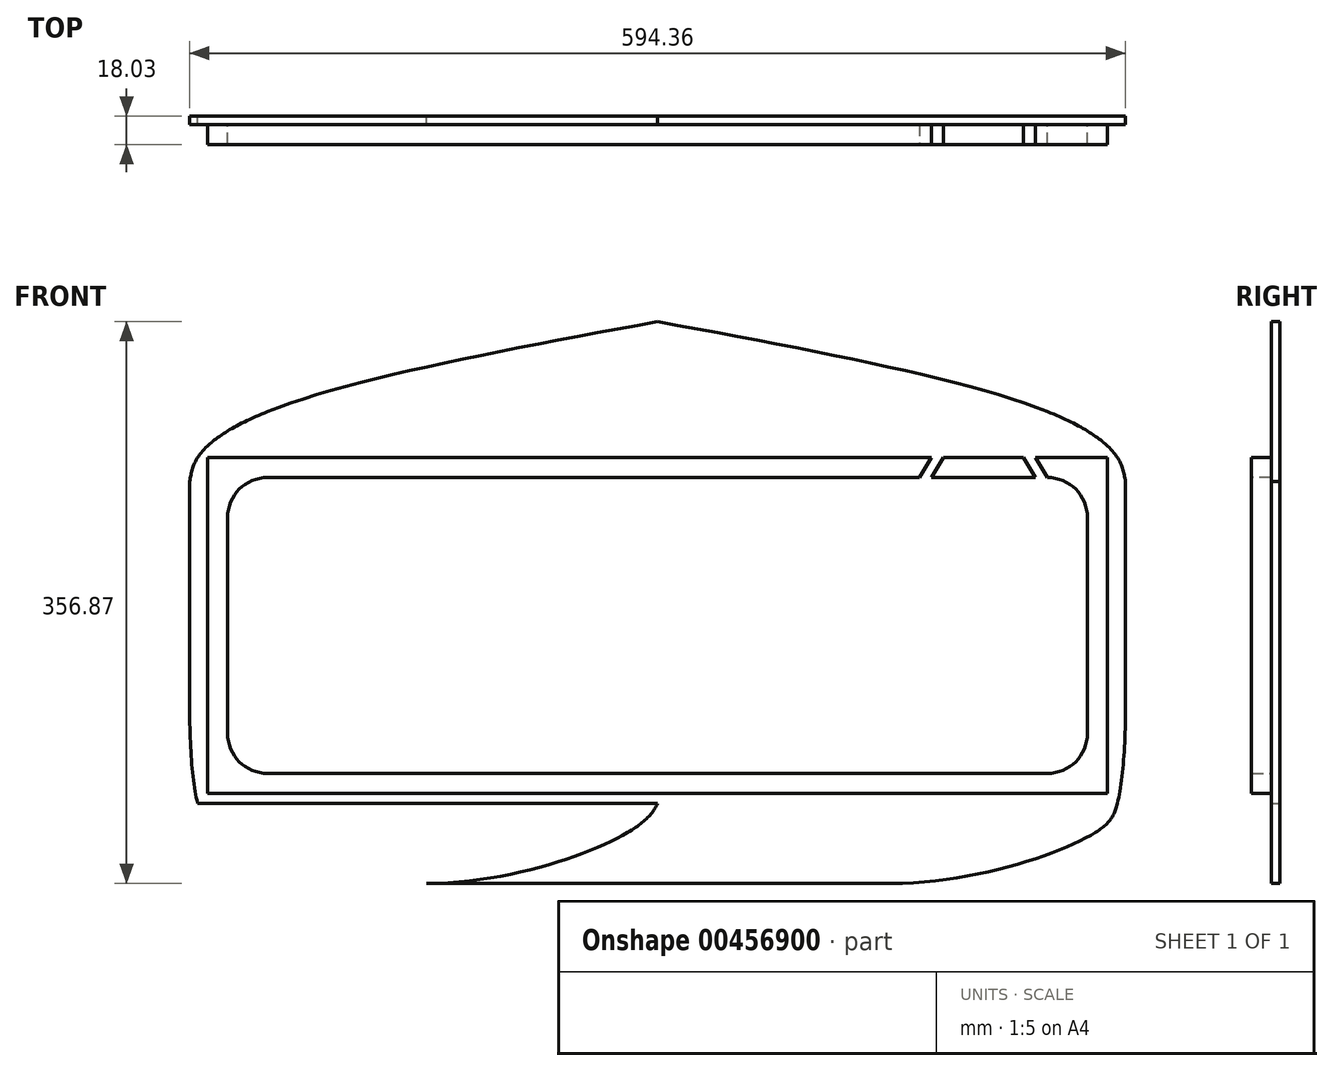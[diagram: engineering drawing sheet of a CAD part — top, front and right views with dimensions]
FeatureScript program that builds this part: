
annotation { "Feature Type Name" : "Feature", "Feature Type Description" : "" }
export const myFeature = defineFeature(function(context is Context, id is Id, definition is map)
    precondition{}
    {
        {
            var Q0;
            Q0=qCreatedBy(makeId("Front.planeOp"),FACE);
            var sketch = newSketch(context, id + "F0", { "sketchPlane" : qUnion([Q0])});
            skLineSegment(sketch, "E0.bottom", {"start": v(0, 0) * mm, "end": v(-584.2, 0) * mm});
            skLineSegment(sketch, "E0.top", {"start": v(0, 219.7) * mm, "end": v(-584.2, 219.7) * mm});
            skLineSegment(sketch, "E0.left", {"start": v(0, 0) * mm, "end": v(0, 219.7) * mm});
            skLineSegment(sketch, "E0.right", {"start": v(-584.2, 0) * mm, "end": v(-584.2, 219.7) * mm});
            skPoint(sketch, "E1", {"position": v(-292.1, 219.7) * mm});
            skSolve(sketch);
        }
        {
            var Q0;
            Q0=makeQuery(id+"F0.imprint","IMPRINT",FACE,{"disambiguationData":[TD([[makeQuery(id+"F0.imprint","IMPRINT",EDGE,{"derivedFrom":sQuery(id+"F0.wireOp",EDGE,"E0.bottom")}),-1.0]])]});
            extrude(context, id + "F1", {"entities" : qUnion([Q0]), "depth" : 5.33 * mm});
        }
        {
            var Q0;
            Q0=makeQuery(id+"F1.opExtrude","CAP_FACE",FACE,{"disambiguationData":[OSD([sQuery(id+"F0.wireOp",EDGE,"E0.bottom"),sQuery(id+"F0.wireOp",EDGE,"E0.top"),sQuery(id+"F0.wireOp",EDGE,"E0.left"),sQuery(id+"F0.wireOp",EDGE,"E0.right")])],"isStart":false});
            var sketch = newSketch(context, id + "F2", { "sketchPlane" : qUnion([Q0])});
            skLineSegment(sketch, "E2", {"start": v(-577.85, 219.7) * mm, "end": v(-577.85, 6.35) * mm});
            skLineSegment(sketch, "E3", {"start": v(-577.85, 6.35) * mm, "end": v(-6.35, 6.35) * mm});
            skLineSegment(sketch, "E4", {"start": v(-6.35, 6.35) * mm, "end": v(-6.35, 219.71) * mm});
            skLineSegment(sketch, "E5", {"start": v(-6.35, 219.71) * mm, "end": v(-577.85, 219.7) * mm});
            skLineSegment(sketch, "E6", {"start": v(-565.15, 207) * mm, "end": v(-565.15, 19.05) * mm});
            skLineSegment(sketch, "E7", {"start": v(-565.15, 19.05) * mm, "end": v(-19.05, 19.05) * mm});
            skLineSegment(sketch, "E8", {"start": v(-19.05, 19.05) * mm, "end": v(-19.05, 207.01) * mm});
            skLineSegment(sketch, "E9", {"start": v(-19.05, 207.01) * mm, "end": v(-565.15, 207) * mm});
            skSolve(sketch);
        }
        {
            var Q0;
            Q0=makeQuery(id+"F2.imprint","IMPRINT",FACE,{"disambiguationData":[TD([[makeQuery(id+"F2.imprint","IMPRINT",EDGE,{"derivedFrom":sQuery(id+"F2.wireOp",EDGE,"E2")}),1.0]])]});
            extrude(context, id + "F3", {"entities" : qUnion([Q0]), "operationType" : NewBodyOperationType.ADD, "depth" : 12.7 * mm});
        }
        {
            var Q0;
            Q0=makeQuery(id+"F3.opExtrude","SWEPT_EDGE",EDGE,{"disambiguationData":[OSD([sQuery(id+"F2.wireOp",EDGE,"E6"),sQuery(id+"F2.wireOp",EDGE,"E9")])]});
            var Q1;
            Q1=makeQuery(id+"F3.opExtrude","SWEPT_EDGE",EDGE,{"disambiguationData":[OSD([sQuery(id+"F2.wireOp",EDGE,"E8"),sQuery(id+"F2.wireOp",EDGE,"E9")])]});
            var Q2;
            Q2=makeQuery(id+"F3.opExtrude","SWEPT_EDGE",EDGE,{"disambiguationData":[OSD([sQuery(id+"F2.wireOp",EDGE,"E7"),sQuery(id+"F2.wireOp",EDGE,"E8")])]});
            var Q3;
            Q3=makeQuery(id+"F3.opExtrude","SWEPT_EDGE",EDGE,{"disambiguationData":[OSD([sQuery(id+"F2.wireOp",EDGE,"E6"),sQuery(id+"F2.wireOp",EDGE,"E7")])]});
            fillet(context, id + "F4", {"entities" : qUnion([Q0, Q1, Q2, Q3]), "radius" : 25.4 * mm, "tangentPropagation" : true, "allowEdgeOverflow" : false});
        }
        {
            var Q0;
            Q0=makeQuery(id+"F3.opExtrude","CAP_FACE",FACE,{"disambiguationData":[OSD([sQuery(id+"F2.wireOp",EDGE,"E2"),sQuery(id+"F2.wireOp",EDGE,"E3"),sQuery(id+"F2.wireOp",EDGE,"E4"),sQuery(id+"F2.wireOp",EDGE,"E5"),sQuery(id+"F2.wireOp",EDGE,"E6"),sQuery(id+"F2.wireOp",EDGE,"E7"),sQuery(id+"F2.wireOp",EDGE,"E8"),sQuery(id+"F2.wireOp",EDGE,"E9")])],"isStart":false});
            var sketch = newSketch(context, id + "F5", { "sketchPlane" : qUnion([Q0])});
            skPoint(sketch, "E10", {"position": v(-118.11, 219.7) * mm});
            skPoint(sketch, "E11", {"position": v(-110.5, 219.7) * mm});
            skPoint(sketch, "E12", {"position": v(-59.69, 219.7) * mm});
            skPoint(sketch, "E13", {"position": v(-52.07, 219.7) * mm});
            skPoint(sketch, "E14", {"position": v(-376.28, 272.75) * mm});
            skPoint(sketch, "E15", {"position": v(-12.7, 0) * mm});
            skPoint(sketch, "E16", {"position": v(-20.32, 0) * mm});
            skLineSegment(sketch, "E17", {"start": v(-20.32, 0) * mm, "end": v(-12.7, 0) * mm});
            skPoint(sketch, "E18", {"position": v(-118.11, 207.01) * mm});
            skPoint(sketch, "E19", {"position": v(-125.73, 207.01) * mm});
            skLineSegment(sketch, "E20", {"start": v(-125.73, 207.01) * mm, "end": v(-118.11, 219.7) * mm});
            skLineSegment(sketch, "E21", {"start": v(-125.73, 207.01) * mm, "end": v(-118.11, 207.01) * mm});
            skLineSegment(sketch, "E22", {"start": v(-118.11, 207.01) * mm, "end": v(-110.5, 219.7) * mm});
            skLineSegment(sketch, "E23", {"start": v(-118.11, 219.7) * mm, "end": v(-110.5, 219.7) * mm});
            skLineSegment(sketch, "E24", {"start": v(-59.69, 219.7) * mm, "end": v(-52.07, 219.7) * mm});
            skLineSegment(sketch, "E25", {"start": v(-110.5, 219.7) * mm, "end": v(-59.69, 219.7) * mm});
            skLineSegment(sketch, "E26", {"start": v(-59.69, 219.7) * mm, "end": v(-110.5, 219.7) * mm});
            skLineSegment(sketch, "E27", {"start": v(-110.5, 219.7) * mm, "end": v(-113.58, 214.56) * mm});
            skPoint(sketch, "E28", {"position": v(-44.45, 207.01) * mm});
            skPoint(sketch, "E29", {"position": v(-52.07, 207.01) * mm});
            skLineSegment(sketch, "E30", {"start": v(-59.69, 219.7) * mm, "end": v(-52.07, 207.01) * mm});
            skLineSegment(sketch, "E31", {"start": v(-52.07, 219.7) * mm, "end": v(-44.45, 207.01) * mm});
            skLineSegment(sketch, "E32", {"start": v(-52.07, 207.01) * mm, "end": v(-44.45, 207.01) * mm});
            skLineSegment(sketch, "E33", {"start": v(-52.07, 219.7) * mm, "end": v(-59.69, 219.7) * mm});
            skPoint(sketch, "E34", {"position": v(-56.6, 214.56) * mm});
            skLineSegment(sketch, "E35", {"start": v(-113.58, 214.56) * mm, "end": v(-56.6, 214.56) * mm});
            skSolve(sketch);
        }
        {
            var Q0;
            Q0=makeQuery(id+"F5.imprint","IMPRINT",FACE,{"disambiguationData":[TD([[makeQuery(id+"F5.imprint","IMPRINT",EDGE,{"derivedFrom":sQuery(id+"F5.wireOp",EDGE,"E20")}),-1.0]])]});
            var Q1;
            {var subQ8=sQuery(id+"F5.wireOp",EDGE,"RZINdJYM-ykuw-GilU-JIjt-DnibDYUsXZuo");Q1=makeQuery(id+"F5.imprint","IMPRINT",FACE,{"disambiguationData":[TD([[makeQuery(id+"F5.imprint","IMPRINT",EDGE,{"derivedFrom":subQ8}),1.0]])]});}
            var Q2;
            Q2=makeQuery(id+"F5.imprint","IMPRINT",FACE,{"disambiguationData":[TD([[makeQuery(id+"F5.imprint","IMPRINT",EDGE,{"derivedFrom":sQuery(id+"F5.wireOp",EDGE,"RZINdJYM-ykuw-GilU-JIjt-DnibDYUsXZuo")}),-1.0]])]});
            var Q3;
            Q3=makeQuery(id+"F5.imprint","IMPRINT",FACE,{"disambiguationData":[TD([[makeQuery(id+"F5.imprint","IMPRINT",EDGE,{"derivedFrom":sQuery(id+"F5.wireOp",EDGE,"NQJIxGkc-Vixr-o2zM-VUe3-bVQ5EoZFKsab")}),1.0]])]});
            var Q4;
            Q4=makeQuery(id+"F5.imprint","IMPRINT",FACE,{"disambiguationData":[TD([[makeQuery(id+"F5.imprint","IMPRINT",EDGE,{"derivedFrom":sQuery(id+"F5.wireOp",EDGE,"E30")}),1.0]])]});
            var Q5;
            {var subQ0=sQuery(id+"F5.wireOp",EDGE,"E26");Q5=makeQuery(id+"F5.imprint","IMPRINT",FACE,{"disambiguationData":[TD([[makeQuery(id+"F5.imprint","IMPRINT",EDGE,{"derivedFrom":subQ0}),1.0]])]});}
            extrude(context, id + "F6", {"entities" : qUnion([Q0, Q1, Q2, Q3, Q4, Q5]), "operationType" : NewBodyOperationType.REMOVE, "oppositeDirection" : true, "depth" : 12.7 * mm});
        }
        {
            var Q0;
            Q0=makeQuery(id+"F1.opExtrude","CAP_FACE",FACE,{"disambiguationData":[OSD([sQuery(id+"F0.wireOp",EDGE,"E0.bottom"),sQuery(id+"F0.wireOp",EDGE,"E0.top"),sQuery(id+"F0.wireOp",EDGE,"E0.left"),sQuery(id+"F0.wireOp",EDGE,"E0.right")])],"isStart":true});
            var sketch = newSketch(context, id + "F7", { "sketchPlane" : qUnion([Q0])});
            skLineSegment(sketch, "E36", {"start": v(0, 0) * mm, "end": v(-5.08, 0) * mm});
            skLineSegment(sketch, "E37", {"start": v(-5.08, 0) * mm, "end": v(-5.08, 229.87) * mm});
            skLineSegment(sketch, "E38", {"start": v(-5.08, 229.87) * mm, "end": v(589.28, 229.87) * mm});
            skLineSegment(sketch, "E39", {"start": v(589.28, 229.87) * mm, "end": v(589.28, 0) * mm});
            skLineSegment(sketch, "E40", {"start": v(589.28, 0) * mm, "end": v(584.2, 0) * mm});
            skPoint(sketch, "E41", {"position": v(589.28, 114.93) * mm});
            skPoint(sketch, "E42", {"position": v(584.2, 109.85) * mm});
            skPoint(sketch, "E43", {"position": v(292.1, 229.87) * mm});
            skPoint(sketch, "E44", {"position": v(292.1, 219.7) * mm});
            skPoint(sketch, "E45", {"position": v(-5.08, 114.94) * mm});
            skPoint(sketch, "E46", {"position": v(0, 109.85) * mm});
            skPoint(sketch, "E47", {"position": v(538.48, 229.87) * mm});
            skPoint(sketch, "E48", {"position": v(45.72, 229.87) * mm});
            skPoint(sketch, "E49", {"position": v(-5.08, 204.47) * mm});
            skPoint(sketch, "E50", {"position": v(589.28, 204.47) * mm});
            skPoint(sketch, "E51", {"position": v(584.2, 183.25) * mm});
            skPoint(sketch, "E52", {"position": v(0, 176.13) * mm});
            skPoint(sketch, "E53", {"position": v(589.28, 63.5) * mm});
            skPoint(sketch, "E54", {"position": v(-5.08, 63.5) * mm});
            skPoint(sketch, "E55", {"position": v(0, 219.7) * mm});
            skPoint(sketch, "E56", {"position": v(584.2, 219.7) * mm});
            skPoint(sketch, "E57", {"position": v(393.7, 219.7) * mm});
            skPoint(sketch, "E58", {"position": v(190.5, 219.7) * mm});
            skLineSegment(sketch, "E59", {"start": v(292.1, 219.7) * mm, "end": v(-5.08, 229.87) * mm});
            skLineSegment(sketch, "E60", {"start": v(292.1, 219.7) * mm, "end": v(589.28, 229.87) * mm});
            skLineSegment(sketch, "E61", {"start": v(589.28, -18.42) * mm, "end": v(-5.08, -18.42) * mm});
            skLineSegment(sketch, "E62", {"start": v(589.28, 0) * mm, "end": v(589.28, -18.42) * mm});
            skLineSegment(sketch, "E63", {"start": v(292.1, 229.87) * mm, "end": v(292.1, 306.07) * mm});
            skPoint(sketch, "E64", {"position": v(292.1, -18.42) * mm});
            skLineSegment(sketch, "E65", {"start": v(589.28, -18.42) * mm, "end": v(589.28, -50.8) * mm});
            skLineSegment(sketch, "E66", {"start": v(589.28, -50.8) * mm, "end": v(292.1, -50.8) * mm});
            skPoint(sketch, "E67", {"position": v(292.1, 0) * mm});
            skPoint(sketch, "E68", {"position": v(440.7, -50.8) * mm});
            skLineSegment(sketch, "E69", {"start": v(292.1, -50.8) * mm, "end": v(-5.08, -50.8) * mm});
            skLineSegment(sketch, "E70", {"start": v(-5.08, -50.8) * mm, "end": v(-5.08, -18.42) * mm});
            skPoint(sketch, "E71", {"position": v(143.51, -50.8) * mm});
            skPoint(sketch, "E72", {"position": v(570.23, -18.42) * mm});
            skPoint(sketch, "E73", {"position": v(13.97, -18.42) * mm});
            skPoint(sketch, "E74", {"position": v(6.35, 219.7) * mm});
            skPoint(sketch, "E75", {"position": v(577.85, 219.7) * mm});
            skPoint(sketch, "E76", {"position": v(6.35, 0) * mm});
            skPoint(sketch, "E77", {"position": v(577.85, 0) * mm});
            skPoint(sketch, "E78", {"position": v(44.45, 229.87) * mm});
            skPoint(sketch, "E79", {"position": v(539.75, 229.87) * mm});
            skLineSegment(sketch, "E80", {"start": v(44.45, 229.87) * mm, "end": v(44.45, 248.92) * mm});
            skLineSegment(sketch, "E81", {"start": v(539.75, 229.87) * mm, "end": v(539.75, 248.92) * mm});
            skLineSegment(sketch, "E82", {"start": v(292.1, 0) * mm, "end": v(292.1, 6.35) * mm});
            skPoint(sketch, "E83", {"position": v(311.15, -18.42) * mm});
            skPoint(sketch, "E84", {"position": v(273.05, -18.42) * mm});
            skLineSegment(sketch, "E85", {"start": v(0, 109.85) * mm, "end": v(-44.45, 109.85) * mm});
            skLineSegment(sketch, "E86", {"start": v(584.2, 109.85) * mm, "end": v(628.65, 109.85) * mm});
            skLineSegment(sketch, "E87", {"start": v(-44.45, 109.85) * mm, "end": v(-44.45, 84.45) * mm});
            skLineSegment(sketch, "E88", {"start": v(-5.08, 0) * mm, "end": v(-5.08, -18.42) * mm});
            skLineSegment(sketch, "E89", {"start": v(628.65, 109.85) * mm, "end": v(628.65, 84.45) * mm});
            skFitSpline(sketch, "E90", {"points": [v(292.1, 0) * mm, v(311.15, -18.42) * mm, v(440.7, -50.8) * mm, v(570.23, -18.42) * mm, v(584.2, 0) * mm, v(589.28, 63.5) * mm], "startDerivative": vector(75.38, -162.05) * mm, "endDerivative": vector(-1.2, 379.78) * mm});
            skFitSpline(sketch, "E91", {"points": [v(292.1, 0) * mm, v(273.05, -18.42) * mm, v(143.51, -50.8) * mm, v(13.97, -18.42) * mm, v(0, 0) * mm, v(-5.08, 63.5) * mm], "startDerivative": vector(-102.03, -153.51) * mm, "endDerivative": vector(1.16, 380.73) * mm});
            skFitSpline(sketch, "E92", {"points": [v(292.1, 306.07) * mm, v(539.75, 248.92) * mm, v(584.2, 219.7) * mm, v(589.28, 204.47) * mm], "startDerivative": vector(500.8, -92.88) * mm, "endDerivative": vector(17.5, -102.22) * mm});
            skFitSpline(sketch, "E93", {"points": [v(292.1, 306.07) * mm, v(44.45, 248.92) * mm, v(0, 219.7) * mm, v(-5.08, 204.47) * mm], "startDerivative": vector(-500.8, -92.88) * mm, "endDerivative": vector(-17.5, -102.22) * mm});
            skSolve(sketch);
        }
        {
            var Q0;
            {var subQ0=sQuery(id+"F7.wireOp",EDGE,"E91");var subQ1=sQuery(id+"F7.wireOp",EDGE,"E61");var subQ2=makeQuery(id+"F7.imprint","INTERSECT",VERTEX,{"disambiguationData":[OD(0.0)],"derivedFrom":[subQ1,subQ0]});Q0=makeQuery(id+"F7.imprint","IMPRINT",FACE,{"disambiguationData":[TD([[makeQuery(id+"F7.imprint","IMPRINT",EDGE,{"disambiguationData":[TD([[subQ2,-1.0]])],"derivedFrom":subQ1}),-1.0]])]});}
            var Q1;
            {var subQ0=sQuery(id+"F7.wireOp",EDGE,"E91");var subQ1=sQuery(id+"F7.wireOp",EDGE,"E61");var subQ2=makeQuery(id+"F7.imprint","INTERSECT",VERTEX,{"disambiguationData":[OD(0.0)],"derivedFrom":[subQ1,subQ0]});Q1=makeQuery(id+"F7.imprint","IMPRINT",FACE,{"disambiguationData":[TD([[makeQuery(id+"F7.imprint","IMPRINT",EDGE,{"disambiguationData":[TD([[subQ2,-1.0]])],"derivedFrom":subQ1}),1.0]])]});}
            var Q2;
            {var subQ0=sQuery(id+"F7.wireOp",EDGE,"E90");var subQ1=sQuery(id+"F7.wireOp",EDGE,"E61");var subQ2=makeQuery(id+"F7.imprint","INTERSECT",VERTEX,{"disambiguationData":[OD(0.0)],"derivedFrom":[subQ1,subQ0]});Q2=makeQuery(id+"F7.imprint","IMPRINT",FACE,{"disambiguationData":[TD([[makeQuery(id+"F7.imprint","IMPRINT",EDGE,{"disambiguationData":[TD([[subQ2,-1.0]])],"derivedFrom":subQ1}),-1.0]])]});}
            var Q3;
            {var subQ0=sQuery(id+"F7.wireOp",EDGE,"E90");var subQ1=sQuery(id+"F7.wireOp",EDGE,"E61");var subQ2=makeQuery(id+"F7.imprint","INTERSECT",VERTEX,{"disambiguationData":[OD(0.0)],"derivedFrom":[subQ1,subQ0]});Q3=makeQuery(id+"F7.imprint","IMPRINT",FACE,{"disambiguationData":[TD([[makeQuery(id+"F7.imprint","IMPRINT",EDGE,{"disambiguationData":[TD([[subQ2,-1.0]])],"derivedFrom":subQ1}),1.0]])]});}
            var Q4;
            {var subQ0=sQuery(id+"F7.wireOp",EDGE,"E91");var subQ3=sQuery(id+"F7.wireOp",EDGE,"E37");var subQ8=makeQuery(id+"F7.imprint","INTERSECT",VERTEX,{"disambiguationData":[OD(0.0)],"derivedFrom":[subQ3,subQ0]});Q4=makeQuery(id+"F7.imprint","IMPRINT",FACE,{"disambiguationData":[TD([[makeQuery(id+"F7.imprint","IMPRINT",EDGE,{"disambiguationData":[TD([[subQ8,1.0]])],"derivedFrom":subQ3}),-1.0]])]});}
            var Q5;
            {var subQ0=sQuery(id+"F7.wireOp",EDGE,"ab0071de-1401-4d7e-944b-b81abdc96300");var subQ1=sQuery(id+"F7.wireOp",EDGE,"E37");var subQ2=makeQuery(id+"F7.imprint","INTERSECT",VERTEX,{"derivedFrom":[subQ1,subQ0]});Q5=makeQuery(id+"F7.imprint","IMPRINT",FACE,{"disambiguationData":[TD([[makeQuery(id+"F7.imprint","IMPRINT",EDGE,{"disambiguationData":[TD([[subQ2,1.0]])],"derivedFrom":subQ1}),-1.0]])]});}
            var Q6;
            {var subQ0=sQuery(id+"F7.wireOp",EDGE,"E59");var subQ3=sQuery(id+"F7.wireOp",EDGE,"ab0071de-1401-4d7e-944b-b81abdc96300");var subQ4=makeQuery(id+"F7.imprint","INTERSECT",VERTEX,{"derivedFrom":[subQ0,subQ3]});Q6=makeQuery(id+"F7.imprint","IMPRINT",FACE,{"disambiguationData":[TD([[makeQuery(id+"F7.imprint","IMPRINT",EDGE,{"disambiguationData":[TD([[subQ4,1.0]])],"derivedFrom":subQ0}),1.0]])]});}
            var Q7;
            {var subQ0=sQuery(id+"F7.wireOp",EDGE,"E80");Q7=makeQuery(id+"F7.imprint","IMPRINT",FACE,{"disambiguationData":[TD([[makeQuery(id+"F7.imprint","IMPRINT",EDGE,{"derivedFrom":subQ0}),1.0]])]});}
            var Q8;
            {var subQ0=sQuery(id+"F7.wireOp",EDGE,"E63");Q8=makeQuery(id+"F7.imprint","IMPRINT",FACE,{"disambiguationData":[TD([[makeQuery(id+"F7.imprint","IMPRINT",EDGE,{"derivedFrom":subQ0}),1.0]])]});}
            var Q9;
            {var subQ0=sQuery(id+"F7.wireOp",EDGE,"E38");var subQ9=makeQuery(id+"F7.imprint","INTERSECT",VERTEX,{"derivedFrom":[subQ0,sQuery(id+"F7.wireOp",EDGE,"E80")]});Q9=makeQuery(id+"F7.imprint","IMPRINT",FACE,{"disambiguationData":[TD([[makeQuery(id+"F7.imprint","IMPRINT",EDGE,{"disambiguationData":[TD([[subQ9,1.0]])],"derivedFrom":subQ0}),-1.0]])]});}
            var Q10;
            {var subQ0=sQuery(id+"F7.wireOp",EDGE,"E63");Q10=makeQuery(id+"F7.imprint","IMPRINT",FACE,{"disambiguationData":[TD([[makeQuery(id+"F7.imprint","IMPRINT",EDGE,{"derivedFrom":subQ0}),-1.0]])]});}
            var Q11;
            {var subQ0=sQuery(id+"F7.wireOp",EDGE,"E60");var subQ3=sQuery(id+"F7.wireOp",EDGE,"17dd5abb-82da-4189-b5be-3d9ac0586960");var subQ4=makeQuery(id+"F7.imprint","INTERSECT",VERTEX,{"derivedFrom":[subQ0,subQ3]});Q11=makeQuery(id+"F7.imprint","IMPRINT",FACE,{"disambiguationData":[TD([[makeQuery(id+"F7.imprint","IMPRINT",EDGE,{"disambiguationData":[TD([[subQ4,1.0]])],"derivedFrom":subQ0}),-1.0]])]});}
            var Q12;
            {var subQ0=sQuery(id+"F7.wireOp",EDGE,"E81");Q12=makeQuery(id+"F7.imprint","IMPRINT",FACE,{"disambiguationData":[TD([[makeQuery(id+"F7.imprint","IMPRINT",EDGE,{"derivedFrom":subQ0}),-1.0]])]});}
            var Q13;
            {var subQ0=sQuery(id+"F7.wireOp",EDGE,"17dd5abb-82da-4189-b5be-3d9ac0586960");var subQ1=sQuery(id+"F7.wireOp",EDGE,"E39");var subQ2=makeQuery(id+"F7.imprint","INTERSECT",VERTEX,{"derivedFrom":[subQ1,subQ0]});Q13=makeQuery(id+"F7.imprint","IMPRINT",FACE,{"disambiguationData":[TD([[makeQuery(id+"F7.imprint","IMPRINT",EDGE,{"disambiguationData":[TD([[subQ2,-1.0]])],"derivedFrom":subQ1}),-1.0]])]});}
            var Q14;
            {var subQ3=sQuery(id+"F7.wireOp",EDGE,"E39");var subQ5=sQuery(id+"F7.wireOp",EDGE,"E90");var subQ6=makeQuery(id+"F7.imprint","INTERSECT",VERTEX,{"disambiguationData":[OD(0.0)],"derivedFrom":[subQ3,subQ5]});Q14=makeQuery(id+"F7.imprint","IMPRINT",FACE,{"disambiguationData":[TD([[makeQuery(id+"F7.imprint","IMPRINT",EDGE,{"disambiguationData":[TD([[subQ6,1.0]])],"derivedFrom":subQ3}),-1.0]])]});}
            var Q15;
            {var subQ0=sQuery(id+"F7.wireOp",EDGE,"E93");var subQ1=sQuery(id+"F7.wireOp",EDGE,"E37");var subQ2=makeQuery(id+"F7.imprint","INTERSECT",VERTEX,{"derivedFrom":[subQ1,subQ0]});Q15=makeQuery(id+"F7.imprint","IMPRINT",FACE,{"disambiguationData":[TD([[makeQuery(id+"F7.imprint","IMPRINT",EDGE,{"disambiguationData":[TD([[subQ2,1.0]])],"derivedFrom":subQ1}),-1.0]])]});}
            var Q16;
            {var subQ0=sQuery(id+"F7.wireOp",EDGE,"E92");var subQ1=sQuery(id+"F7.wireOp",EDGE,"E39");var subQ2=makeQuery(id+"F7.imprint","INTERSECT",VERTEX,{"derivedFrom":[subQ1,subQ0]});Q16=makeQuery(id+"F7.imprint","IMPRINT",FACE,{"disambiguationData":[TD([[makeQuery(id+"F7.imprint","IMPRINT",EDGE,{"disambiguationData":[TD([[subQ2,-1.0]])],"derivedFrom":subQ1}),-1.0]])]});}
            extrude(context, id + "F8", {"entities" : qUnion([Q0, Q1, Q2, Q3, Q4, Q5, Q6, Q7, Q8, Q9, Q10, Q11, Q12, Q13, Q14, Q15, Q16]), "operationType" : NewBodyOperationType.ADD, "oppositeDirection" : true, "depth" : 5.33 * mm});
        }
    });
